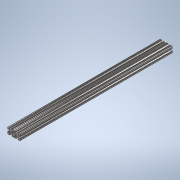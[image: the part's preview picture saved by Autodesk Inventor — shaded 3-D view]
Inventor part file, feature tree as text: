
AUTODESK INVENTOR PART (.ipt)
format: ipt  version: 2020 (Build 240168000, 168)  size: 354,816 bytes
history: native  units: in
note: dims shown in document units (in); Inventor stores cm internally (conversion verified against a paired STEP export)
features: sketch x2, extrude x1
ambient origin geometry x8: Origin, YZ Plane, XZ Plane, XY Plane, X Axis, Y Axis, Z Axis, Center Point
bodies: Solid1 (feature_tree)
feature tree (3):
  extrude  "Extrusion1"  [1 undecoded]
  sketch  "Sketch2"
  sketch  "Sketch1"  dims[d0=24.0in d1=0.0in]
note: 1 required parameter value undecoded (feature->parameter linkage not recoverable at this tier; creation-order binding heuristic only, values carry confidence <= 0.55)
